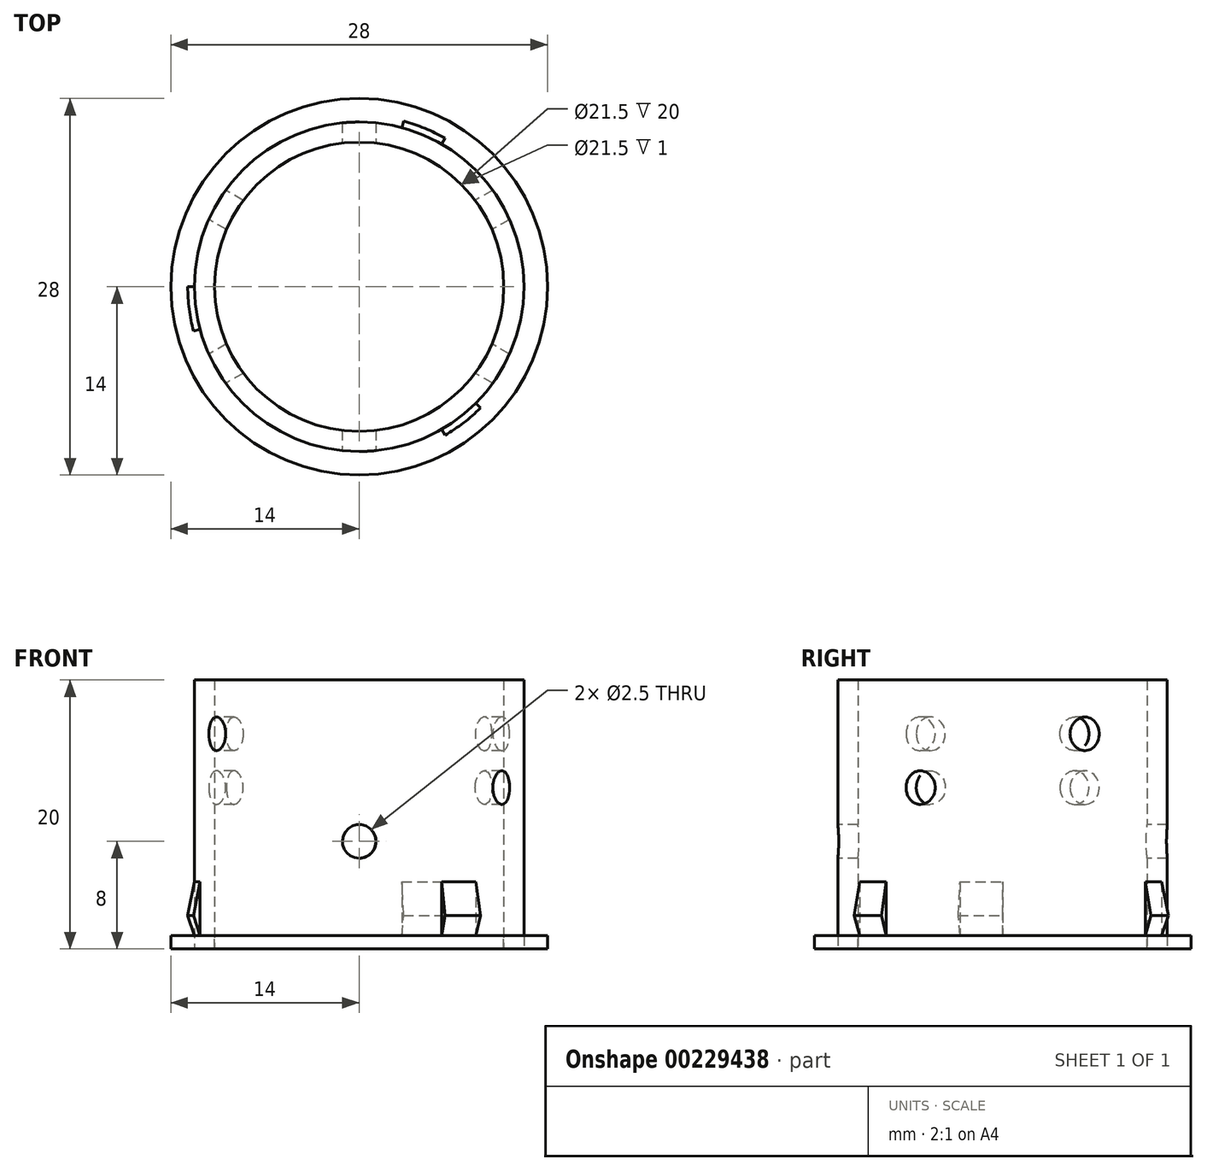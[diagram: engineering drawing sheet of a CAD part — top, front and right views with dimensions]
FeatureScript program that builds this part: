
annotation { "Feature Type Name" : "Feature", "Feature Type Description" : "" }
export const myFeature = defineFeature(function(context is Context, id is Id, definition is map)
    precondition{}
    {
        {
            var Q0;
            Q0=qCreatedBy(makeId("Top.planeOp"),FACE);
            var sketch = newSketch(context, id + "F0", { "sketchPlane" : qUnion([Q0])});
            skCircle(sketch, "E0", {"center": v(0, 0) * mm, "radius": 14 * mm});
            skSolve(sketch);
        }
        {
            var Q0;
            Q0=makeQuery(id+"F0.imprint","IMPRINT",FACE,{"disambiguationData":[TD([[makeQuery(id+"F0.imprint","IMPRINT",EDGE,{"derivedFrom":sQuery(id+"F0.wireOp",EDGE,"E0")}),1.0]])]});
            extrude(context, id + "F1", {"entities" : qUnion([Q0]), "depth" : 1 * mm});
        }
        {
            var Q0;
            Q0=qCreatedBy(makeId("Top.planeOp"),FACE);
            var sketch = newSketch(context, id + "F2", { "sketchPlane" : qUnion([Q0])});
            skCircle(sketch, "E1", {"center": v(0, 0) * mm, "radius": 12.25 * mm});
            skSolve(sketch);
        }
        {
            var Q0;
            Q0 = qSketchRegion(id + "F2", true);
            var Q1;
            Q1=sQuery(id+"F2.wireOp",EDGE,"E1");
            extrude(context, id + "F3", {"entities" : qUnion([Q0]), "surfaceEntities" : qUnion([Q1]), "depth" : 20 * mm});
        }
        {
            var Q0;
            Q0=qCreatedBy(makeId("Top.planeOp"),FACE);
            cPlane(context, id + "F4", {"entities" : qUnion([Q0]), "cplaneType" : CPlaneType.OFFSET, "offset" : 1 * mm, "width" : 150 * mm, "height" : 150 * mm});
        }
        {
            var Q0;
            Q0=qCreatedBy(id+"F4.planeOp",FACE);
            var sketch = newSketch(context, id + "F5", { "sketchPlane" : qUnion([Q0])});
            skCircle(sketch, "E2", {"center": v(0, 0) * mm, "radius": 10.75 * mm});
            skSolve(sketch);
        }
        {
            var Q0;
            Q0 = qSketchRegion(id + "F5", true);
            extrude(context, id + "F6", {"entities" : qUnion([Q0]), "operationType" : NewBodyOperationType.REMOVE, "offsetDistance" : 25 * mm, "depth" : 25 * mm});
        }
        {
            var Q0;
            Q0=qCreatedBy(makeId("Front.planeOp"),FACE);
            var sketch = newSketch(context, id + "F7", { "sketchPlane" : qUnion([Q0])});
            skLineSegment(sketch, "E3", {"start": v(0, 0) * mm, "end": v(0, 56.56) * mm});
            skSolve(sketch);
        }
        {
            var Q0;
            Q0=sQuery(id+"F7.wireOp",EDGE,"E3");
            var Q1;
            Q1=qCreatedBy(makeId("Front.planeOp"),FACE);
            cPlane(context, id + "F8", {"entities" : qUnion([Q0, Q1]), "cplaneType" : CPlaneType.LINE_ANGLE, "offset" : 25 * mm, "angle" : 60 * degree, "width" : 150 * mm, "height" : 150 * mm});
        }
        {
            var Q0;
            Q0=sQuery(id+"F7.wireOp",EDGE,"E3");
            var Q1;
            Q1=qCreatedBy(makeId("Front.planeOp"),FACE);
            cPlane(context, id + "F9", {"entities" : qUnion([Q0, Q1]), "cplaneType" : CPlaneType.LINE_ANGLE, "offset" : 25 * mm, "angle" : 120 * degree, "width" : 150 * mm, "height" : 150 * mm});
        }
        {
            var Q0;
            Q0=qCreatedBy(makeId("Front.planeOp"),FACE);
            var sketch = newSketch(context, id + "F10", { "sketchPlane" : qUnion([Q0])});
            skCircle(sketch, "E4", {"center": v(0, 8) * mm, "radius": 1.25 * mm});
            skSolve(sketch);
        }
        {
            var Q0;
            Q0 = qSketchRegion(id + "F10", true);
            extrude(context, id + "F11", {"entities" : qUnion([Q0]), "operationType" : NewBodyOperationType.REMOVE, "endBound" : BoundingType.THROUGH_ALL, "oppositeDirection" : true, "depth" : 25 * mm, "hasSecondDirection" : true, "secondDirectionOppositeDirection" : false, "secondDirectionDepth" : 25 * mm});
        }
        {
            var Q0;
            Q0=qCreatedBy(id+"F8.planeOp",FACE);
            var sketch = newSketch(context, id + "F12", { "sketchPlane" : qUnion([Q0])});
            skCircle(sketch, "E5", {"center": v(0, 12) * mm, "radius": 1.25 * mm});
            skSolve(sketch);
        }
        {
            var Q0;
            Q0 = qSketchRegion(id + "F12", true);
            extrude(context, id + "F13", {"entities" : qUnion([Q0]), "operationType" : NewBodyOperationType.REMOVE, "oppositeDirection" : true, "depth" : 25 * mm, "hasSecondDirection" : true, "secondDirectionOppositeDirection" : false, "secondDirectionDepth" : 25 * mm});
        }
        {
            var Q0;
            Q0=qCreatedBy(id+"F9.planeOp",FACE);
            var sketch = newSketch(context, id + "F14", { "sketchPlane" : qUnion([Q0])});
            skCircle(sketch, "E6", {"center": v(0, 16) * mm, "radius": 1.25 * mm});
            skSolve(sketch);
        }
        {
            var Q0;
            Q0 = qSketchRegion(id + "F14", true);
            extrude(context, id + "F15", {"entities" : qUnion([Q0]), "operationType" : NewBodyOperationType.REMOVE, "oppositeDirection" : true, "depth" : 25 * mm, "hasSecondDirection" : true, "secondDirectionOppositeDirection" : false, "secondDirectionDepth" : 25 * mm});
        }
        {
            var Q0;
            Q0 = qSketchRegion(id + "F5", true);
            extrude(context, id + "F16", {"entities" : qUnion([Q0]), "operationType" : NewBodyOperationType.REMOVE, "oppositeDirection" : true, "depth" : 10 * mm});
        }
        {
            var Q0;
            Q0=qCreatedBy(makeId("Front.planeOp"),FACE);
            var sketch = newSketch(context, id + "F17", { "sketchPlane" : qUnion([Q0])});
            skLineSegment(sketch, "E7", {"start": v(-12.25, 1) * mm, "end": v(-12.75, 2.5) * mm});
            skLineSegment(sketch, "E8", {"start": v(-12.75, 2.5) * mm, "end": v(-12.25, 5) * mm});
            skLineSegment(sketch, "E9", {"start": v(-12.25, 5) * mm, "end": v(-12.25, 1) * mm});
            skSolve(sketch);
        }
        {
            var Q0;
            Q0=makeQuery(id+"F17.imprint","IMPRINT",FACE,{"disambiguationData":[TD([[makeQuery(id+"F17.imprint","IMPRINT",EDGE,{"derivedFrom":sQuery(id+"F17.wireOp",EDGE,"E7")}),-1.0]])]});
            var Q1;
            Q1=sQuery(id+"F17.wireOp",EDGE,"E9");
            var Q2;
            Q2=sQuery(id+"F17.wireOp",EDGE,"E8");
            var Q3;
            Q3=sQuery(id+"F17.wireOp",EDGE,"E7");
            var Q4;
            Q4=sQuery(id+"F7.wireOp",EDGE,"E3");
            revolve(context, id + "F18", {"entities" : qUnion([Q0]), "surfaceEntities" : qUnion([Q1, Q2, Q3]), "axis" : qUnion([Q4]), "revolveType" : RevolveType.ONE_DIRECTION, "angle" : 15 * degree});
        }
        {
            var Q0;
            Q0=makeQuery(id+"F18.opRevolve","SWEPT_BODY",BODY,{"disambiguationData":[OSD([sQuery(id+"F17.wireOp",EDGE,"E7"),sQuery(id+"F17.wireOp",EDGE,"E8"),sQuery(id+"F17.wireOp",EDGE,"E9")])]});
            var Q1;
            Q1=sQuery(id+"F7.wireOp",EDGE,"E3");
            circularPattern(context, id + "F19", {"entities" : qUnion([Q0]), "axis" : qUnion([Q1]), "angle" : 360 * degree, "instanceCount" : 3, "equalSpace" : true});
        }
    });
